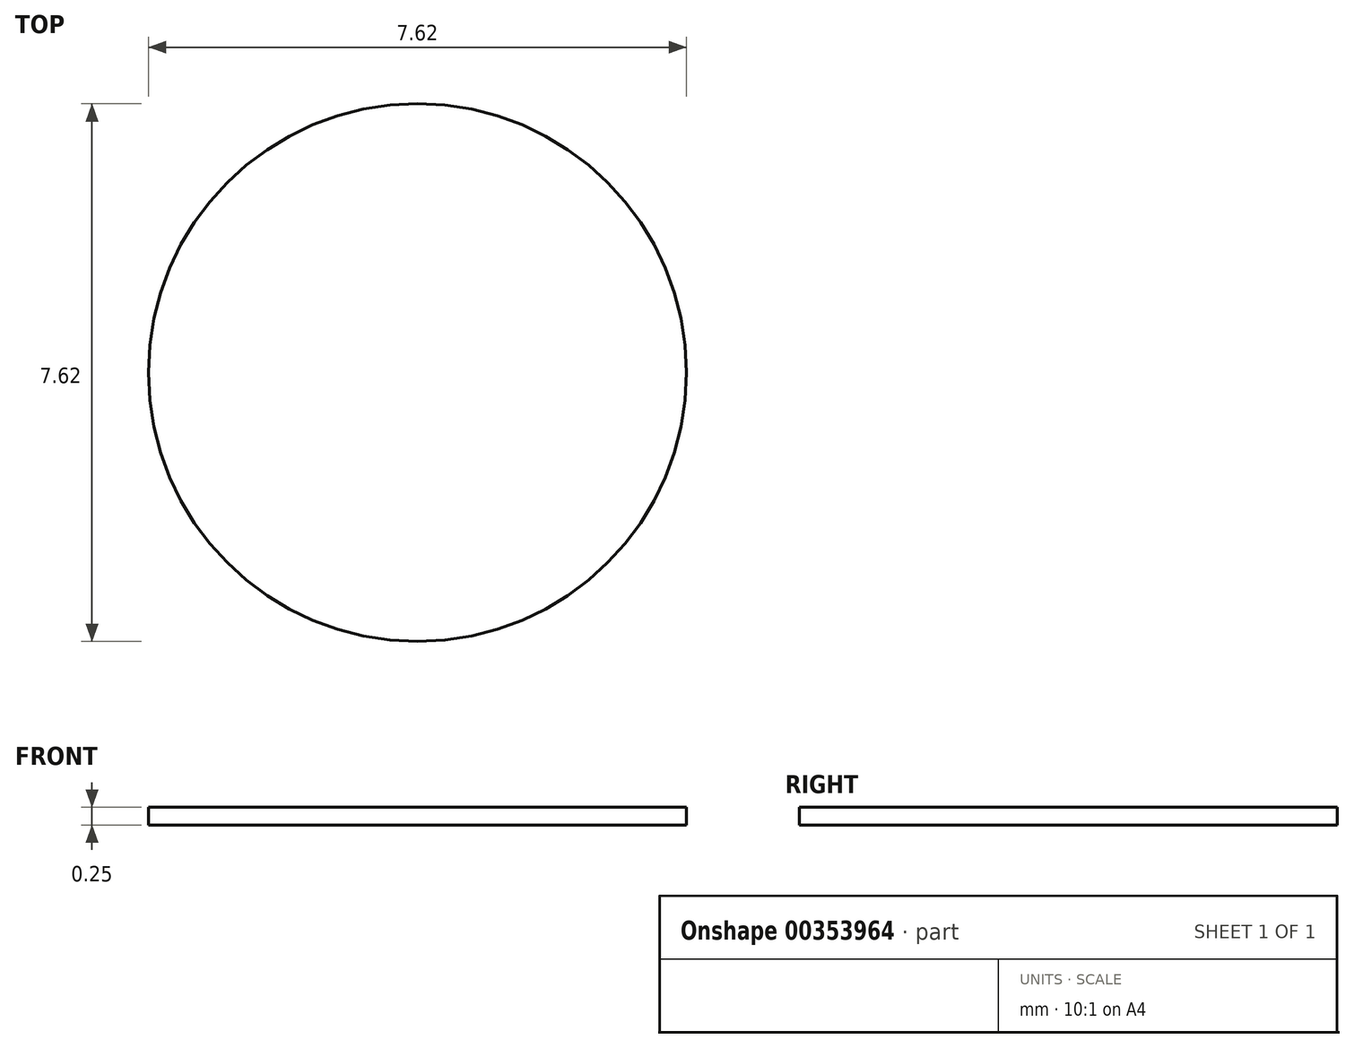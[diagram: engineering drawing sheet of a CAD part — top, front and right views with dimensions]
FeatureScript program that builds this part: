
annotation { "Feature Type Name" : "Feature", "Feature Type Description" : "" }
export const myFeature = defineFeature(function(context is Context, id is Id, definition is map)
    precondition{}
    {
        {
            var Q0;
            Q0=qCreatedBy(makeId("Top.planeOp"),FACE);
            var sketch = newSketch(context, id + "F0", { "sketchPlane" : qUnion([Q0])});
            skCircle(sketch, "E0", {"center": v(0, 0) * mm, "radius": 3.81 * mm});
            skSolve(sketch);
        }
        {
            var Q0;
            Q0 = qSketchRegion(id + "F0", true);
            extrude(context, id + "F1", {"entities" : qUnion([Q0]), "depth" : 0.25 * mm});
        }
    });
